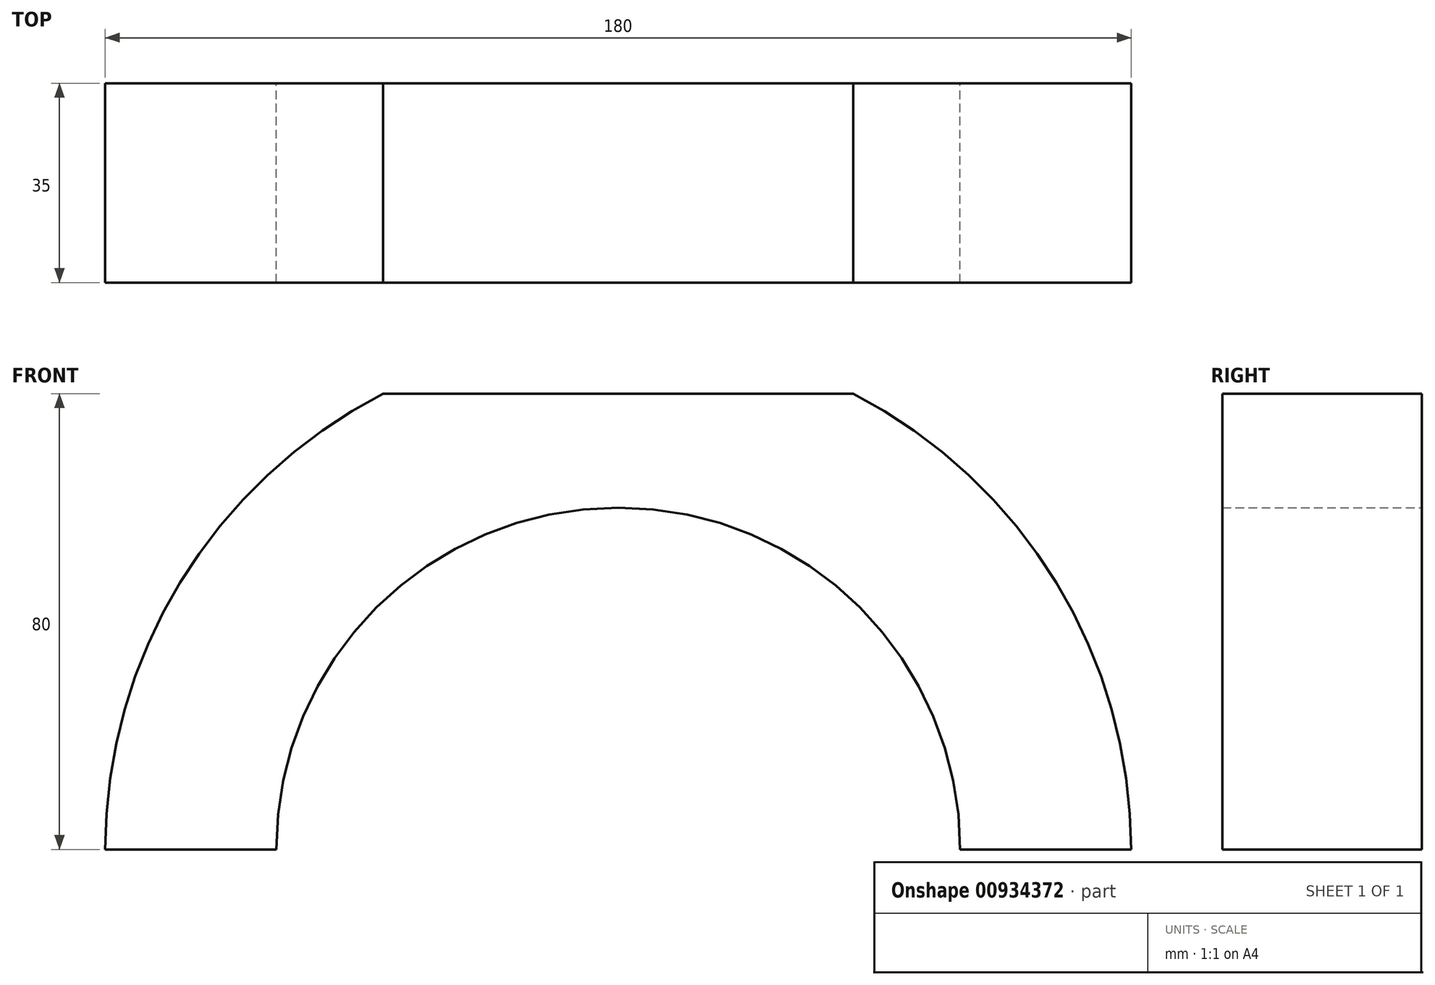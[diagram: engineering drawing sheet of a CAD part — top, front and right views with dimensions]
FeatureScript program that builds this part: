
annotation { "Feature Type Name" : "Feature", "Feature Type Description" : "" }
export const myFeature = defineFeature(function(context is Context, id is Id, definition is map)
    precondition{}
    {
        {
            var Q0;
            Q0=qCreatedBy(makeId("Front.planeOp"),FACE);
            var sketch = newSketch(context, id + "F0", { "sketchPlane" : qUnion([Q0])});
            skArc(sketch, "E0", {"start": v(60, 0) * mm, "mid": v(0, 60) * mm, "end": v(-60, 0) * mm});
            skArc(sketch, "E1.0", {"start": v(90, 0) * mm, "mid": v(76.85, 46.85) * mm, "end": v(41.23, 80) * mm});
            skLineSegment(sketch, "E2", {"start": v(-60, 0) * mm, "end": v(-90, 0) * mm});
            skLineSegment(sketch, "E3", {"start": v(60, 0) * mm, "end": v(90, 0) * mm});
            skPoint(sketch, "E4.orphan", {"position": v(-40.64, 0) * mm});
            skPoint(sketch, "E5.orphan", {"position": v(47.84, 0) * mm});
            skLineSegment(sketch, "E6", {"start": v(-41.23, 80) * mm, "end": v(41.23, 80) * mm});
            skArc(sketch, "E7.trimOffspring", {"start": v(-41.23, 80) * mm, "mid": v(-76.85, 46.85) * mm, "end": v(-90, 0) * mm});
            skSolve(sketch);
        }
        {
            var Q0;
            Q0 = qSketchRegion(id + "F0", true);
            extrude(context, id + "F1", {"entities" : qUnion([Q0]), "depth" : 10 * mm, "offsetDistance" : 25 * mm, "hasSecondDirection" : true, "secondDirectionOppositeDirection" : true, "secondDirectionDepth" : 25 * mm});
        }
    });
